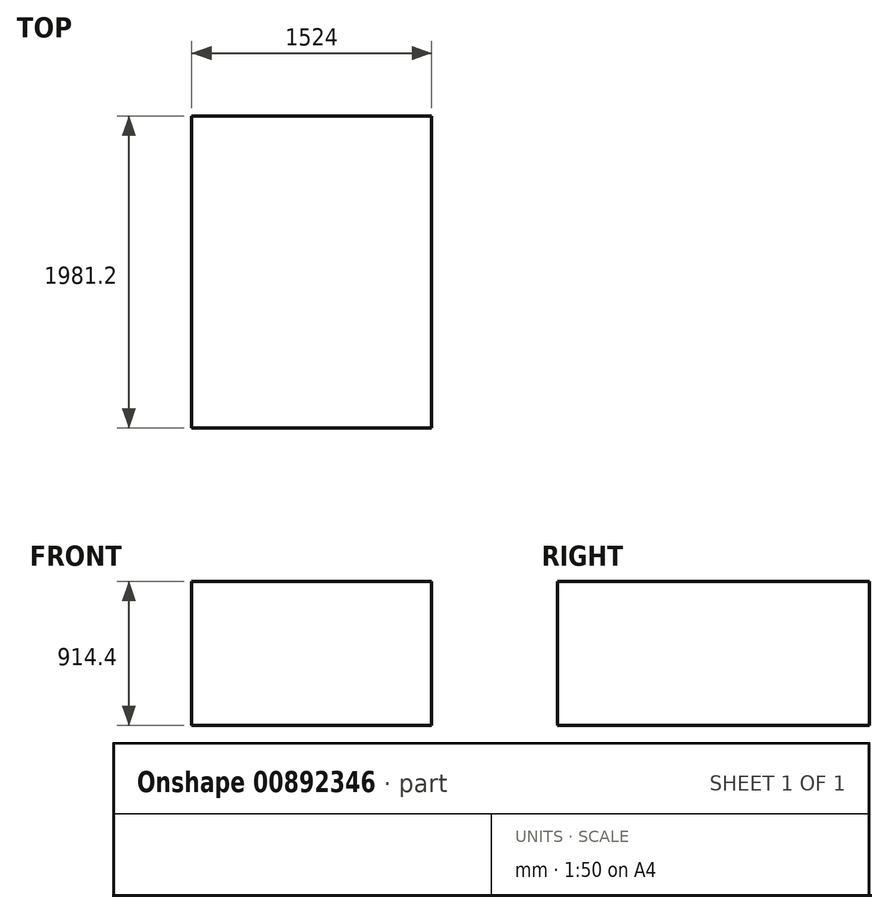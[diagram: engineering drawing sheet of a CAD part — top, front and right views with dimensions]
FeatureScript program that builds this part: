
annotation { "Feature Type Name" : "Feature", "Feature Type Description" : "" }
export const myFeature = defineFeature(function(context is Context, id is Id, definition is map)
    precondition{}
    {
        {
            var Q0;
            Q0=qCreatedBy(makeId("Top.planeOp"),FACE);
            var sketch = newSketch(context, id + "F0", { "sketchPlane" : qUnion([Q0])});
            skLineSegment(sketch, "E0.bottom", {"start": v(-762, 990.6) * mm, "end": v(762, 990.6) * mm});
            skLineSegment(sketch, "E0.top", {"start": v(-762, -990.6) * mm, "end": v(762, -990.6) * mm});
            skLineSegment(sketch, "E0.left", {"start": v(-762, 990.6) * mm, "end": v(-762, -990.6) * mm});
            skLineSegment(sketch, "E0.right", {"start": v(762, 990.6) * mm, "end": v(762, -990.6) * mm});
            skPoint(sketch, "E0.middle", {"position": v(0, 0) * mm});
            skSolve(sketch);
        }
        {
            var Q0;
            Q0 = qSketchRegion(id + "F0", true);
            extrude(context, id + "F1", {"entities" : qUnion([Q0]), "depth" : 914.4 * mm, "offsetDistance" : 25.4 * mm});
        }
    });
